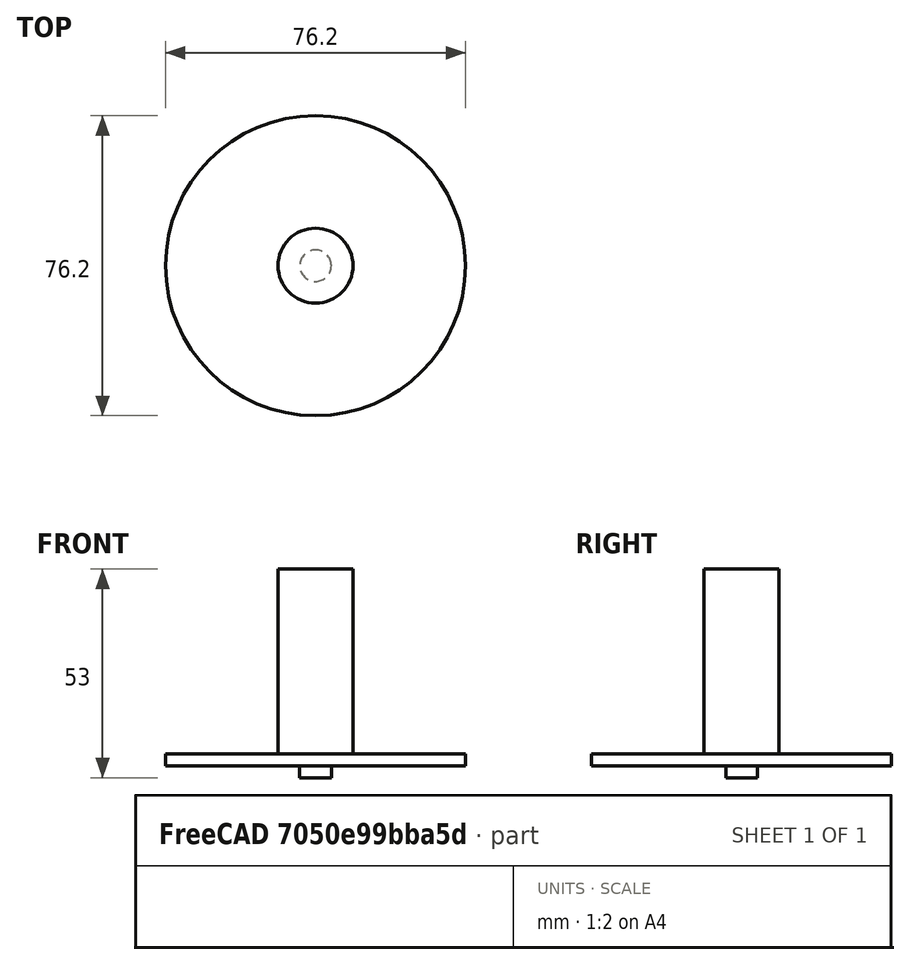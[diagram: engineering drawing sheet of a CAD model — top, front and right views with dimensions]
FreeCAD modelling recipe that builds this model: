
FCSTD DOCUMENT  (FreeCAD 0.19R24049 (Git))
Label: slittingsaw
License: All rights reserved
LicenseURL: http://en.wikipedia.org/wiki/All_rights_reserved
objects: Sketcher::SketchObject×1, PartDesign::Revolution×1, App::FeaturePython×1, PartDesign::Body×1
note: 4 computed .brp shape members not serialized (recipe doc carries the construction recipe); baked Part::Feature solids carry a one-line shape summary decoded from their .brp

FEATURE [Sketcher::SketchObject] Sketch
  FullyConstrained = true
  MapMode = 5
  Placement = pos=(0,0,0) rot=(1,0,0;1.5708rad)
  Support = -> [XZ_Plane]
  expr: Constraints[11] = <<Attributes>>.ShankDiameter
  expr: Constraints[5] = <<Attributes>>.Length
  expr: Constraints[24] = <<Attributes>>.BladeThickness
  expr: Constraints[23] = <<Attributes>>.CapHeight
  expr: Constraints[25] = <<Attributes>>.Diameter
  expr: Constraints[21] = <<Attributes>>.CapDiameter
  sketch-geometry (11):
    g0: LineSegment StartX=0 StartY=0 StartZ=0 EndX=0 EndY=-53 EndZ=0
    g1: LineSegment StartX=9.525 StartY=0 StartZ=0 EndX=0 EndY=0 EndZ=0
    g2: LineSegment StartX=38.1 StartY=-50 StartZ=0 EndX=-38.1 EndY=-50 EndZ=0
    g3: LineSegment StartX=9.525 StartY=-47 StartZ=0 EndX=38.1 EndY=-47 EndZ=0
    g4: LineSegment StartX=9.525 StartY=0 StartZ=0 EndX=9.525 EndY=-47 EndZ=0
    g5: LineSegment StartX=-9.525 StartY=2.3057e-12 StartZ=0 EndX=9.525 EndY=0 EndZ=0
    g6: LineSegment StartX=38.1 StartY=-47 StartZ=0 EndX=38.1 EndY=-50 EndZ=0
    g7: LineSegment StartX=38.1 StartY=-50 StartZ=0 EndX=4 EndY=-50 EndZ=0
    g8: LineSegment StartX=4 StartY=-50 StartZ=0 EndX=4 EndY=-53 EndZ=0
    g9: LineSegment StartX=4 StartY=-53 StartZ=0 EndX=0 EndY=-53 EndZ=0
    g10: LineSegment StartX=-4 StartY=-53 StartZ=0 EndX=4 EndY=-53 EndZ=0
  constraints (29):
    c: Vertical(g0)
    c: Horizontal(g1)
    c: Coincident(g0,g1)
    c: Coincident(g0,g-1)
    c: Symmetric(g6,g2,g0)
    c: DistanceY(g6,g1) = 50
    c: Horizontal(g3)
    c: Vertical(g4)
    c: Coincident(g1,g4)
    c: Symmetric(g5,g5,g0)
    c: Coincident(g5,g1)
    c: DistanceX(g5,g5) = 19.05
    c: Coincident(g3,g4)
    c: Coincident(g3,g6)
    c: Vertical(g6)
    c: Coincident(g6,g7)
    c: Horizontal(g7)
    c: Coincident(g8,g9)
    c: Horizontal(g9)
    c: Vertical(g8)
    c: Coincident(g10,g8)
    c: DistanceX(g10,g10) = 8
    c: Symmetric(g10,g8,g-2)
    c: DistanceY(g8,g8) = 3
    c: DistanceY(g6,g6) = 3
    c: DistanceX(g2,g2) = 76.2
    c: Coincident(g7,g8)
    c: Coincident(g2,g6)
    c: Coincident(g0,g9)
FEATURE [PartDesign::Revolution] Revolution
  AllowMultiFace = false
  Angle = 360
  Axis = (0,-2e-16,1)
  Base = (0,0,0)
  Placement = pos=(0,0,0) rot=(1,0,0;1.5708rad)
  Profile = -> Sketch
  ReferenceAxis = -> Sketch [V_Axis]
  Reversed = true
FEATURE [App::FeaturePython] PropertyBag  label="Attributes"  # WARN: FeaturePython — macro-defined, semantics opaque (R4)
  BladeThickness = 3
  CapDiameter = 8
  CapHeight = 3
  Chipload = 0
  CustomPropertyGroups = Shape | Attributes
  Diameter = 76.2
  Flutes = 0
  Length = 50
  Material = 0
  ShankDiameter = 19.05
FEATURE [PartDesign::Body] Body  label="SlittingSaw"
  Group = -> [Sketch,Revolution,PropertyBag]
  Origin = -> Origin
  Tip = -> Revolution
